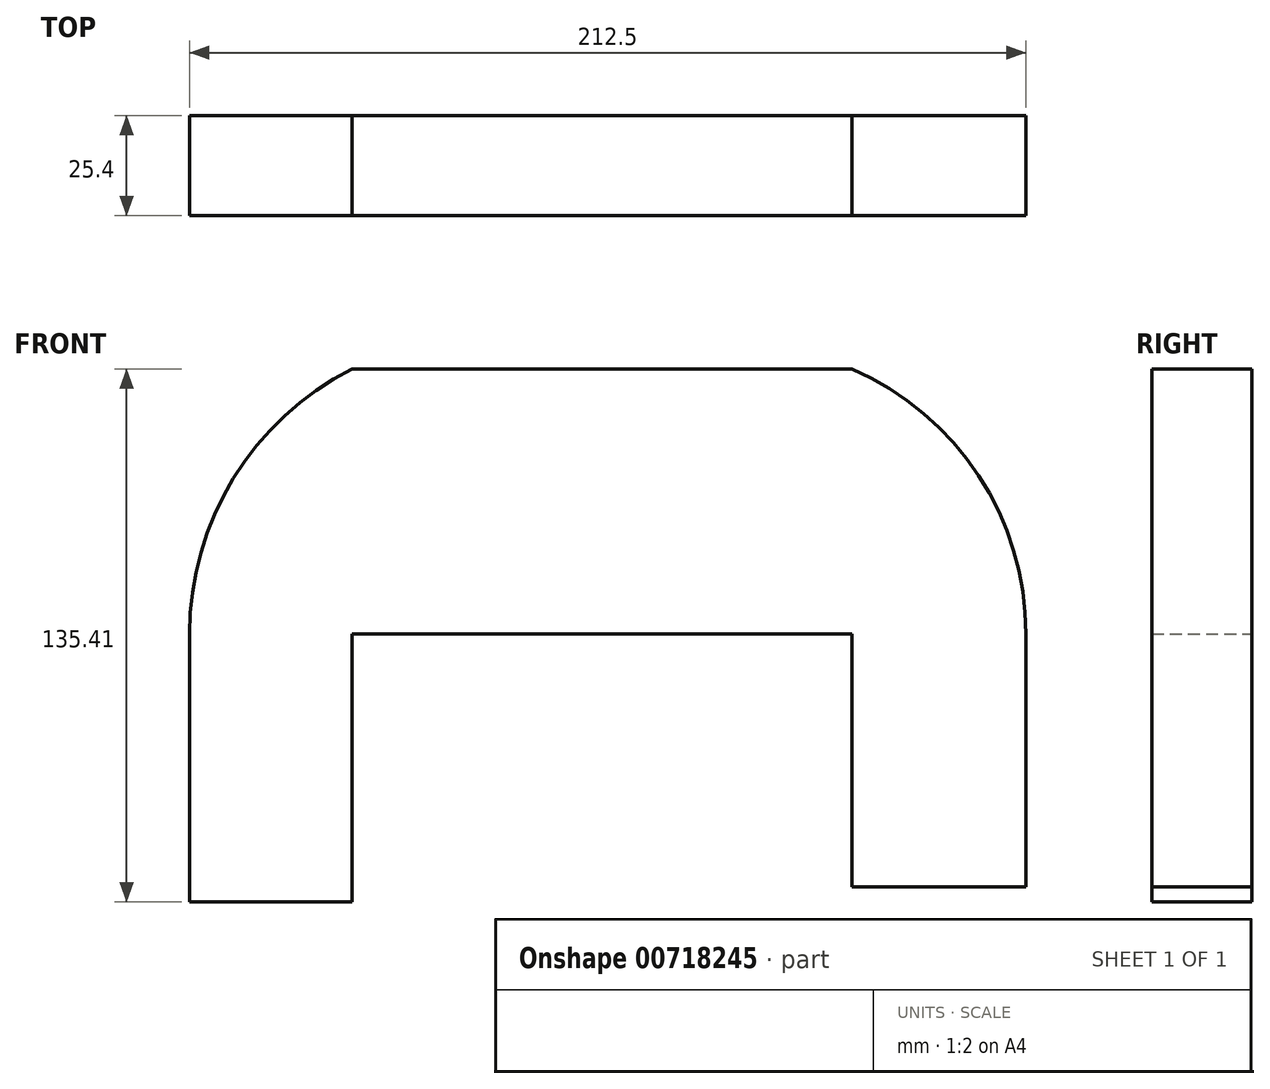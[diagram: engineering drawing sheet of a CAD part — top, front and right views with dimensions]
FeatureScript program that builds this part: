
annotation { "Feature Type Name" : "Feature", "Feature Type Description" : "" }
export const myFeature = defineFeature(function(context is Context, id is Id, definition is map)
    precondition{}
    {
        {
            var Q0;
            Q0=qCreatedBy(makeId("Front.planeOp"),FACE);
            var sketch = newSketch(context, id + "F0", { "sketchPlane" : qUnion([Q0])});
            skLineSegment(sketch, "E0.bottom", {"start": v(0, 0) * mm, "end": v(-127, 0) * mm});
            skLineSegment(sketch, "E0.top", {"start": v(0, 67.32) * mm, "end": v(-127, 67.32) * mm});
            skLineSegment(sketch, "E0.left", {"start": v(0, 0) * mm, "end": v(0, 67.32) * mm});
            skLineSegment(sketch, "E0.right", {"start": v(-127, 0) * mm, "end": v(-127, 67.32) * mm});
            skLineSegment(sketch, "E1.bottom", {"start": v(-127, 0) * mm, "end": v(-168.24, 0) * mm});
            skLineSegment(sketch, "E1.top", {"start": v(-127, -68.1) * mm, "end": v(-168.24, -68.1) * mm});
            skLineSegment(sketch, "E1.left", {"start": v(-127, 0) * mm, "end": v(-127, -68.1) * mm});
            skLineSegment(sketch, "E1.right", {"start": v(-168.24, 0) * mm, "end": v(-168.24, -68.1) * mm});
            skArc(sketch, "E2", {"start": v(-127, 67.32) * mm, "mid": v(-157.11, 39.48) * mm, "end": v(-168.24, 0) * mm});
            skLineSegment(sketch, "E3.bottom", {"start": v(0, 0) * mm, "end": v(44.26, 0) * mm});
            skLineSegment(sketch, "E3.top", {"start": v(0, -64.3) * mm, "end": v(44.26, -64.3) * mm});
            skLineSegment(sketch, "E3.left", {"start": v(0, 0) * mm, "end": v(0, -64.3) * mm});
            skLineSegment(sketch, "E3.right", {"start": v(44.26, 0) * mm, "end": v(44.26, -64.3) * mm});
            skArc(sketch, "E4", {"start": v(44.26, 0) * mm, "mid": v(32.2, 40.28) * mm, "end": v(0, 67.32) * mm});
            skSolve(sketch);
        }
        {
            var Q0;
            Q0 = qSketchRegion(id + "F0", true);
            extrude(context, id + "F1", {"entities" : qUnion([Q0]), "depth" : 25.4 * mm, "offsetDistance" : 25.4 * mm});
        }
    });
